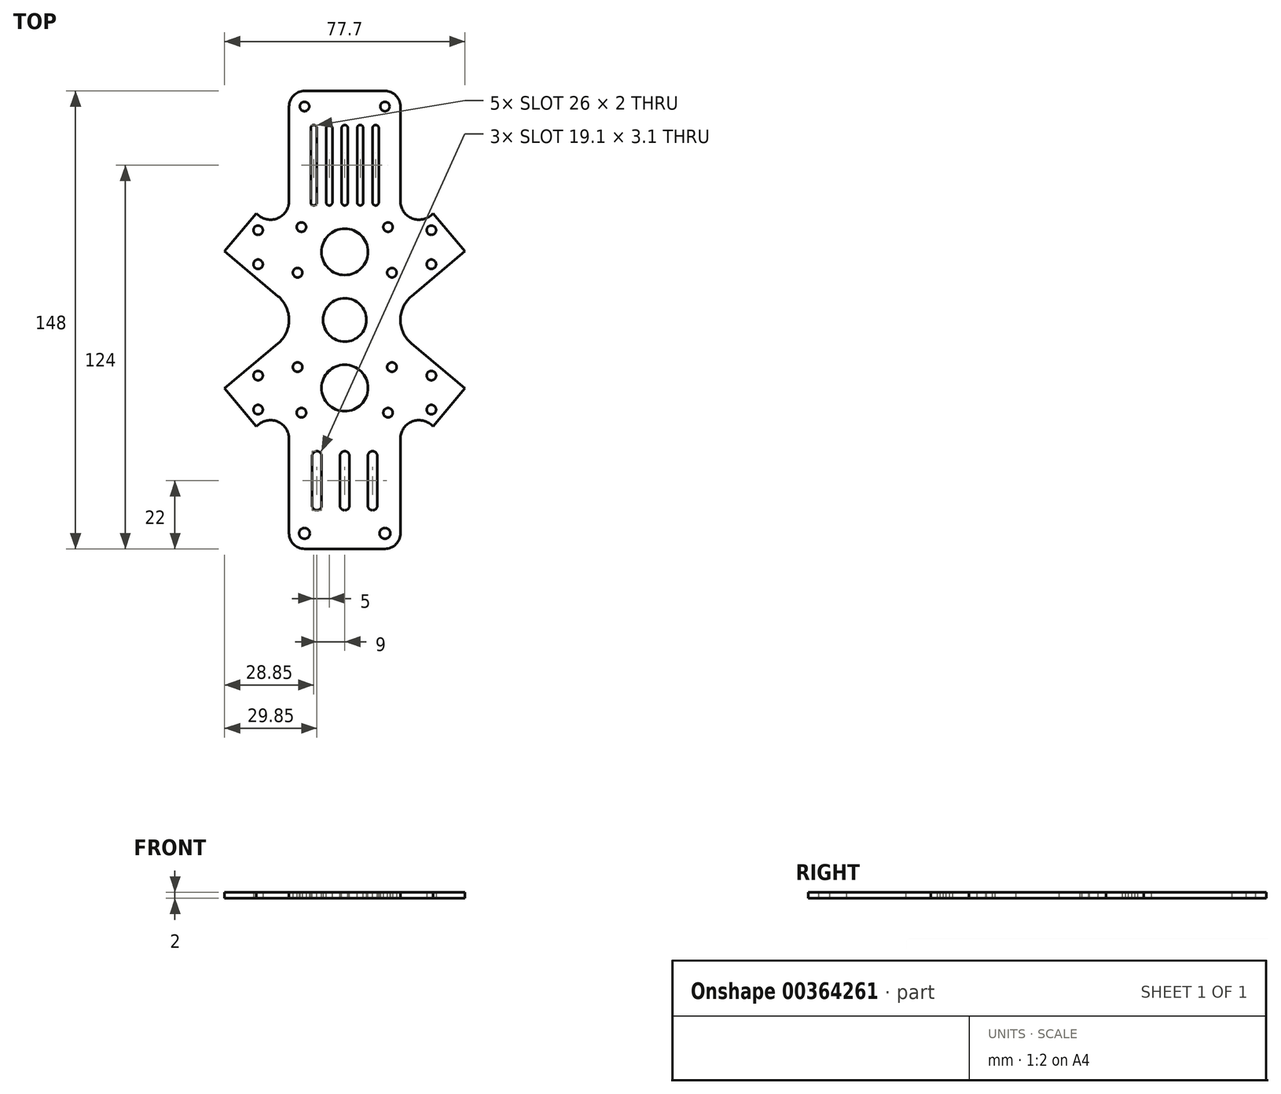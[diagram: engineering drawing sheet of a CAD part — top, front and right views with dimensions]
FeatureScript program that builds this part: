
annotation { "Feature Type Name" : "Feature", "Feature Type Description" : "" }
export const myFeature = defineFeature(function(context is Context, id is Id, definition is map)
    precondition{}
    {
        {
            var Q0;
            Q0=qCreatedBy(makeId("Top.planeOp"),FACE);
            var sketch = newSketch(context, id + "F0", { "sketchPlane" : qUnion([Q0])});
            skLineSegment(sketch, "E0", {"start": v(-28.56, 34.41) * mm, "end": v(-38.85, 22.15) * mm});
            skLineSegment(sketch, "E1", {"start": v(-38.85, 22.15) * mm, "end": v(-21.58, 7.66) * mm});
            skLineSegment(sketch, "E2", {"start": v(-28.56, 34.41) * mm, "end": v(-27.86, 33.82) * mm});
            skLineSegment(sketch, "E3", {"start": v(0, 74) * mm, "end": v(-13, 74) * mm});
            skLineSegment(sketch, "E4", {"start": v(-18, 69) * mm, "end": v(-18, 38.41) * mm});
            skLineSegment(sketch, "E5", {"start": v(-84.26, 70.7) * mm, "end": v(0, 0) * mm, "construction": true});
            skCircle(sketch, "E6", {"center": v(0, 0) * mm, "radius": 110 * mm, "construction": true});
            skPoint(sketch, "E7.visualSharp", {"position": v(-18, 25.55) * mm});
            skArc(sketch, "E7.filletArc", {"start": v(-27.86, 33.82) * mm, "mid": v(-21.46, 32.98) * mm, "end": v(-18, 38.41) * mm});
            skPoint(sketch, "E8.visualSharp", {"position": v(-18, 74) * mm});
            skArc(sketch, "E8.filletArc", {"start": v(-13, 74) * mm, "mid": v(-16.54, 72.54) * mm, "end": v(-18, 69) * mm});
            skCircle(sketch, "E9", {"center": v(-13, 69) * mm, "radius": 1.52 * mm});
            skCircle(sketch, "E10", {"center": v(-28, 29) * mm, "radius": 1.52 * mm});
            skCircle(sketch, "E11", {"center": v(-28, 18) * mm, "radius": 1.52 * mm});
            skCircle(sketch, "E12", {"center": v(-15.25, 15.25) * mm, "radius": 1.52 * mm});
            skCircle(sketch, "E13.MirrorC", {"center": v(13, 69) * mm, "radius": 1.52 * mm});
            skArc(sketch, "E14.MirrorCS", {"start": v(13, 74) * mm, "mid": v(16.54, 72.54) * mm, "end": v(18, 69) * mm});
            skLineSegment(sketch, "E15.MirrorCS", {"start": v(0, 74) * mm, "end": v(13, 74) * mm});
            skCircle(sketch, "E16.MirrorC", {"center": v(28, 29) * mm, "radius": 1.52 * mm});
            skCircle(sketch, "E17.MirrorC", {"center": v(15.25, 15.25) * mm, "radius": 1.52 * mm});
            skCircle(sketch, "E18.MirrorC", {"center": v(28, 18) * mm, "radius": 1.52 * mm});
            skPoint(sketch, "E19.MirrorP", {"position": v(18, 25.55) * mm});
            skLineSegment(sketch, "E20.MirrorCS", {"start": v(28.56, 34.41) * mm, "end": v(38.85, 22.15) * mm});
            skLineSegment(sketch, "E21.MirrorCS", {"start": v(18, 69) * mm, "end": v(18, 38.41) * mm});
            skLineSegment(sketch, "E22.MirrorCS", {"start": v(38.85, 22.15) * mm, "end": v(21.58, 7.66) * mm});
            skLineSegment(sketch, "E23.MirrorCS", {"start": v(28.56, 34.41) * mm, "end": v(27.86, 33.82) * mm});
            skArc(sketch, "E24.MirrorCS", {"start": v(27.86, 33.82) * mm, "mid": v(21.46, 32.98) * mm, "end": v(18, 38.41) * mm});
            skPoint(sketch, "E25.MirrorP", {"position": v(18, 74) * mm});
            skLineSegment(sketch, "E26.MirrorCS", {"start": v(84.26, 70.7) * mm, "end": v(0, 0) * mm, "construction": true});
            skArc(sketch, "E27.MirrorCS", {"start": v(-13, -74) * mm, "mid": v(-16.54, -72.54) * mm, "end": v(-18, -69) * mm});
            skCircle(sketch, "E28.MirrorC", {"center": v(-28, -18) * mm, "radius": 1.52 * mm});
            skCircle(sketch, "E29.MirrorC", {"center": v(28, -29) * mm, "radius": 1.52 * mm});
            skCircle(sketch, "E30.MirrorC", {"center": v(-15.25, -15.25) * mm, "radius": 1.52 * mm});
            skCircle(sketch, "E31.MirrorC", {"center": v(15.25, -15.25) * mm, "radius": 1.52 * mm});
            skLineSegment(sketch, "E32.MirrorCS", {"start": v(0, -74) * mm, "end": v(-13, -74) * mm});
            skCircle(sketch, "E33.MirrorC", {"center": v(28, -18) * mm, "radius": 1.52 * mm});
            skArc(sketch, "E34.MirrorCS", {"start": v(13, -74) * mm, "mid": v(16.54, -72.54) * mm, "end": v(18, -69) * mm});
            skCircle(sketch, "E35.MirrorC", {"center": v(-28, -29) * mm, "radius": 1.52 * mm});
            skPoint(sketch, "E36.MirrorP", {"position": v(-18, -25.55) * mm});
            skArc(sketch, "E37.MirrorCS", {"start": v(-27.86, -33.82) * mm, "mid": v(-21.46, -32.98) * mm, "end": v(-18, -38.41) * mm});
            skArc(sketch, "E38.MirrorCS", {"start": v(27.86, -33.82) * mm, "mid": v(21.46, -32.98) * mm, "end": v(18, -38.41) * mm});
            skLineSegment(sketch, "E39.MirrorCS", {"start": v(-38.85, -22.15) * mm, "end": v(-21.58, -7.66) * mm});
            skLineSegment(sketch, "E40.MirrorCS", {"start": v(0, -74) * mm, "end": v(13, -74) * mm});
            skPoint(sketch, "E41.MirrorP", {"position": v(18, -25.55) * mm});
            skPoint(sketch, "E42.MirrorP", {"position": v(18, -74) * mm});
            skLineSegment(sketch, "E43.MirrorCS", {"start": v(-28.56, -34.41) * mm, "end": v(-27.86, -33.82) * mm});
            skPoint(sketch, "E44.MirrorP", {"position": v(-18, -74) * mm});
            skLineSegment(sketch, "E45.MirrorCS", {"start": v(-18, -69) * mm, "end": v(-18, -38.41) * mm});
            skLineSegment(sketch, "E46.MirrorCS", {"start": v(18, -69) * mm, "end": v(18, -38.41) * mm});
            skLineSegment(sketch, "E47.MirrorCS", {"start": v(38.85, -22.15) * mm, "end": v(21.58, -7.66) * mm});
            skLineSegment(sketch, "E48.MirrorCS", {"start": v(28.56, -34.41) * mm, "end": v(38.85, -22.15) * mm});
            skLineSegment(sketch, "E49.MirrorCS", {"start": v(-28.56, -34.41) * mm, "end": v(-38.85, -22.15) * mm});
            skLineSegment(sketch, "E50.MirrorCS", {"start": v(28.56, -34.41) * mm, "end": v(27.86, -33.82) * mm});
            skPoint(sketch, "E51.visualSharp", {"position": v(-12.45, 0) * mm});
            skArc(sketch, "E51.filletArc", {"start": v(-21.58, -7.66) * mm, "mid": v(-18, 0) * mm, "end": v(-21.58, 7.66) * mm});
            skPoint(sketch, "E52.visualSharp", {"position": v(12.45, 0) * mm});
            skArc(sketch, "E52.filletArc", {"start": v(21.58, 7.66) * mm, "mid": v(18, 0) * mm, "end": v(21.58, -7.66) * mm});
            skCircle(sketch, "E53", {"center": v(-84.26, 70.7) * mm, "radius": 64.5 * mm, "construction": true});
            skCircle(sketch, "E54", {"center": v(-14, 30) * mm, "radius": 1.52 * mm});
            skCircle(sketch, "E55.MirrorC", {"center": v(14, 30) * mm, "radius": 1.52 * mm});
            skCircle(sketch, "E56.MirrorC", {"center": v(-14, -30) * mm, "radius": 1.52 * mm});
            skCircle(sketch, "E57.MirrorC", {"center": v(14, -30) * mm, "radius": 1.52 * mm});
            skCircle(sketch, "E58", {"center": v(-13, -69) * mm, "radius": 1.75 * mm});
            skCircle(sketch, "E59.MirrorC", {"center": v(13, -69) * mm, "radius": 1.75 * mm});
            skCircle(sketch, "E60", {"center": v(0, 0) * mm, "radius": 7 * mm});
            skSolve(sketch);
        }
        {
            var Q0;
            Q0 = qSketchRegion(id + "F0", true);
            extrude(context, id + "F1", {"entities" : qUnion([Q0]), "depth" : 2 * mm});
        }
        {
            var Q0;
            Q0=makeQuery(id+"F1.opExtrude","CAP_FACE",FACE,{"disambiguationData":[OSD([sQuery(id+"F0.wireOp",EDGE,"E0"),sQuery(id+"F0.wireOp",EDGE,"E1"),sQuery(id+"F0.wireOp",EDGE,"E2"),sQuery(id+"F0.wireOp",EDGE,"E3"),sQuery(id+"F0.wireOp",EDGE,"E4"),sQuery(id+"F0.wireOp",EDGE,"E7.filletArc"),sQuery(id+"F0.wireOp",EDGE,"E8.filletArc"),sQuery(id+"F0.wireOp",EDGE,"E9"),sQuery(id+"F0.wireOp",EDGE,"E10"),sQuery(id+"F0.wireOp",EDGE,"E11"),sQuery(id+"F0.wireOp",EDGE,"E12"),sQuery(id+"F0.wireOp",EDGE,"E13.MirrorC"),sQuery(id+"F0.wireOp",EDGE,"E14.MirrorCS"),sQuery(id+"F0.wireOp",EDGE,"E15.MirrorCS"),sQuery(id+"F0.wireOp",EDGE,"E16.MirrorC"),sQuery(id+"F0.wireOp",EDGE,"E17.MirrorC"),sQuery(id+"F0.wireOp",EDGE,"E18.MirrorC"),sQuery(id+"F0.wireOp",EDGE,"E20.MirrorCS"),sQuery(id+"F0.wireOp",EDGE,"E21.MirrorCS"),sQuery(id+"F0.wireOp",EDGE,"E22.MirrorCS"),sQuery(id+"F0.wireOp",EDGE,"E23.MirrorCS"),sQuery(id+"F0.wireOp",EDGE,"E24.MirrorCS"),sQuery(id+"F0.wireOp",EDGE,"E27.MirrorCS"),sQuery(id+"F0.wireOp",EDGE,"E28.MirrorC"),sQuery(id+"F0.wireOp",EDGE,"E29.MirrorC"),sQuery(id+"F0.wireOp",EDGE,"E30.MirrorC"),sQuery(id+"F0.wireOp",EDGE,"E31.MirrorC"),sQuery(id+"F0.wireOp",EDGE,"E32.MirrorCS"),sQuery(id+"F0.wireOp",EDGE,"E33.MirrorC"),sQuery(id+"F0.wireOp",EDGE,"E34.MirrorCS"),sQuery(id+"F0.wireOp",EDGE,"E35.MirrorC"),sQuery(id+"F0.wireOp",EDGE,"E37.MirrorCS"),sQuery(id+"F0.wireOp",EDGE,"E38.MirrorCS"),sQuery(id+"F0.wireOp",EDGE,"E39.MirrorCS"),sQuery(id+"F0.wireOp",EDGE,"E40.MirrorCS"),sQuery(id+"F0.wireOp",EDGE,"E43.MirrorCS"),sQuery(id+"F0.wireOp",EDGE,"E45.MirrorCS"),sQuery(id+"F0.wireOp",EDGE,"E46.MirrorCS"),sQuery(id+"F0.wireOp",EDGE,"E47.MirrorCS"),sQuery(id+"F0.wireOp",EDGE,"E48.MirrorCS"),sQuery(id+"F0.wireOp",EDGE,"E49.MirrorCS"),sQuery(id+"F0.wireOp",EDGE,"E50.MirrorCS"),sQuery(id+"F0.wireOp",EDGE,"E51.filletArc"),sQuery(id+"F0.wireOp",EDGE,"E52.filletArc"),sQuery(id+"F0.wireOp",EDGE,"E54"),sQuery(id+"F0.wireOp",EDGE,"E55.MirrorC"),sQuery(id+"F0.wireOp",EDGE,"E56.MirrorC"),sQuery(id+"F0.wireOp",EDGE,"E57.MirrorC"),sQuery(id+"F0.wireOp",EDGE,"93c6d2c4-f13a-42fa-8daf-070bf65a8a60.0.left"),sQuery(id+"F0.wireOp",EDGE,"93c6d2c4-f13a-42fa-8daf-070bf65a8a60.0.right"),sQuery(id+"F0.wireOp",EDGE,"93c6d2c4-f13a-42fa-8daf-070bf65a8a60.1.left"),sQuery(id+"F0.wireOp",EDGE,"93c6d2c4-f13a-42fa-8daf-070bf65a8a60.1.right"),sQuery(id+"F0.wireOp",EDGE,"E58"),sQuery(id+"F0.wireOp",EDGE,"E59.MirrorC"),sQuery(id+"F0.wireOp",EDGE,"E60"),sQuery(id+"F0.wireOp",EDGE,"nUquFca2-qsaJ-jwJN-5oFK-tLH4V0bp0isj"),sQuery(id+"F0.wireOp",EDGE,"GrDH1Zwj-MUL8-2ccp-gC30-TyDLYz1ijxhj"),sQuery(id+"F0.wireOp",EDGE,"lQEg5da1-VNvQ-DT9M-XKNg-c66ZYZLATFQq"),sQuery(id+"F0.wireOp",EDGE,"kMfInx9H-W6u4-GL8q-Tmun-flGKoSWlkOP9"),sQuery(id+"F0.wireOp",EDGE,"hAw3ivOI-FHfI-7WR2-swgj-VFjn3qP7wQiq"),sQuery(id+"F0.wireOp",EDGE,"v5kMoyw8-5eYl-1tFt-IAkN-Yu3lpjZkXJHz"),sQuery(id+"F0.wireOp",EDGE,"L4HZwAwQ-pxIO-Uqwo-2Bf3-76P6cPw9qCx9"),sQuery(id+"F0.wireOp",EDGE,"TBTr9jrp-s2Nj-AiS6-Zdoc-dO8zuvt9AdQ4"),sQuery(id+"F0.wireOp",EDGE,"8gbrVnR2-a2jK-DphX-z2TC-3oRPmb43RnOK"),sQuery(id+"F0.wireOp",EDGE,"ZJLvlH0n-JZwF-yflx-Rwd1-jo0cSRqBPjVH"),sQuery(id+"F0.wireOp",EDGE,"PCCi1lkv-C6qh-hLjU-n2um-C6nXSVXEERcv"),sQuery(id+"F0.wireOp",EDGE,"3Ri7i5VD-pUbN-ChsC-X1DZ-rpwYTm5fkQc2"),sQuery(id+"F0.wireOp",EDGE,"63a17562-372a-4be2-8eea-18665176cc5a0.MirrorCS"),sQuery(id+"F0.wireOp",EDGE,"63a17562-372a-4be2-8eea-18665176cc5a1.MirrorCS"),sQuery(id+"F0.wireOp",EDGE,"63a17562-372a-4be2-8eea-18665176cc5a2.MirrorCS"),sQuery(id+"F0.wireOp",EDGE,"63a17562-372a-4be2-8eea-18665176cc5a3.MirrorCS"),sQuery(id+"F0.wireOp",EDGE,"63a17562-372a-4be2-8eea-18665176cc5a4.MirrorCS"),sQuery(id+"F0.wireOp",EDGE,"63a17562-372a-4be2-8eea-18665176cc5a5.MirrorCS"),sQuery(id+"F0.wireOp",EDGE,"63a17562-372a-4be2-8eea-18665176cc5a6.MirrorCS"),sQuery(id+"F0.wireOp",EDGE,"63a17562-372a-4be2-8eea-18665176cc5a7.MirrorCS"),sQuery(id+"F0.wireOp",EDGE,"63a17562-372a-4be2-8eea-18665176cc5a8.MirrorCS"),sQuery(id+"F0.wireOp",EDGE,"63a17562-372a-4be2-8eea-18665176cc5a9.MirrorCS"),sQuery(id+"F0.wireOp",EDGE,"63a17562-372a-4be2-8eea-18665176cc5a10.MirrorCS"),sQuery(id+"F0.wireOp",EDGE,"63a17562-372a-4be2-8eea-18665176cc5a11.MirrorCS"),sQuery(id+"F0.wireOp",EDGE,"63a17562-372a-4be2-8eea-18665176cc5a12.MirrorCS"),sQuery(id+"F0.wireOp",EDGE,"63a17562-372a-4be2-8eea-18665176cc5a13.MirrorCS"),sQuery(id+"F0.wireOp",EDGE,"63a17562-372a-4be2-8eea-18665176cc5a16.MirrorCS"),sQuery(id+"F0.wireOp",EDGE,"63a17562-372a-4be2-8eea-18665176cc5a17.MirrorCS")])],"isStart":false});
            var sketch = newSketch(context, id + "F2", { "sketchPlane" : qUnion([Q0])});
            skCircle(sketch, "E61", {"center": v(0, -22) * mm, "radius": 7.5 * mm});
            skCircle(sketch, "E62", {"center": v(0, 22) * mm, "radius": 7.5 * mm});
            skLineSegment(sketch, "E63", {"start": v(-18, 50) * mm, "end": v(18, 50) * mm, "construction": true});
            skLineSegment(sketch, "E64", {"start": v(-9, -44) * mm, "end": v(-9, -60) * mm, "construction": true});
            skLineSegment(sketch, "E65", {"start": v(0, -44) * mm, "end": v(0, -60) * mm, "construction": true});
            skLineSegment(sketch, "E66", {"start": v(9, -44) * mm, "end": v(9, -60) * mm, "construction": true});
            skArc(sketch, "E67.0.startCap", {"start": v(-10.55, -44) * mm, "mid": v(-9, -42.45) * mm, "end": v(-7.45, -44) * mm});
            skArc(sketch, "E67.0.endCap", {"start": v(-7.45, -60) * mm, "mid": v(-9, -61.55) * mm, "end": v(-10.55, -60) * mm});
            skLineSegment(sketch, "E67.0.left", {"start": v(-7.45, -44) * mm, "end": v(-7.45, -60) * mm});
            skLineSegment(sketch, "E67.0.right", {"start": v(-10.55, -44) * mm, "end": v(-10.55, -60) * mm});
            skArc(sketch, "E68.0.startCap", {"start": v(-1.55, -44) * mm, "mid": v(0, -42.45) * mm, "end": v(1.55, -44) * mm});
            skArc(sketch, "E68.0.endCap", {"start": v(1.55, -60) * mm, "mid": v(0, -61.55) * mm, "end": v(-1.55, -60) * mm});
            skLineSegment(sketch, "E68.0.left", {"start": v(1.55, -44) * mm, "end": v(1.55, -60) * mm});
            skLineSegment(sketch, "E68.0.right", {"start": v(-1.55, -44) * mm, "end": v(-1.55, -60) * mm});
            skArc(sketch, "E68.1.startCap", {"start": v(7.45, -44) * mm, "mid": v(9, -42.45) * mm, "end": v(10.55, -44) * mm});
            skArc(sketch, "E68.1.endCap", {"start": v(10.55, -60) * mm, "mid": v(9, -61.55) * mm, "end": v(7.45, -60) * mm});
            skLineSegment(sketch, "E68.1.left", {"start": v(10.55, -44) * mm, "end": v(10.55, -60) * mm});
            skLineSegment(sketch, "E68.1.right", {"start": v(7.45, -44) * mm, "end": v(7.45, -60) * mm});
            skLineSegment(sketch, "E69", {"start": v(-10, 62) * mm, "end": v(-10, 38) * mm, "construction": true});
            skLineSegment(sketch, "E70.1.0.0", {"start": v(-5, 62) * mm, "end": v(-5, 38) * mm, "construction": true});
            skLineSegment(sketch, "E70.2.0.0", {"start": v(0, 62) * mm, "end": v(0, 38) * mm, "construction": true});
            skLineSegment(sketch, "E70.3.0.0", {"start": v(5, 62) * mm, "end": v(5, 38) * mm, "construction": true});
            skLineSegment(sketch, "E70.4.0.0", {"start": v(10, 62) * mm, "end": v(10, 38) * mm, "construction": true});
            skLineSegment(sketch, "E70.direction1", {"start": v(-10, 38) * mm, "end": v(-5, 38) * mm, "construction": true});
            skArc(sketch, "E71.0.startCap", {"start": v(-11, 62) * mm, "mid": v(-10, 63) * mm, "end": v(-9, 62) * mm});
            skArc(sketch, "E71.0.endCap", {"start": v(-9, 38) * mm, "mid": v(-10, 37) * mm, "end": v(-11, 38) * mm});
            skLineSegment(sketch, "E71.0.left", {"start": v(-9, 62) * mm, "end": v(-9, 38) * mm});
            skLineSegment(sketch, "E71.0.right", {"start": v(-11, 62) * mm, "end": v(-11, 38) * mm});
            skArc(sketch, "E72.0.startCap", {"start": v(-6, 62) * mm, "mid": v(-5, 63) * mm, "end": v(-4, 62) * mm});
            skArc(sketch, "E72.0.endCap", {"start": v(-4, 38) * mm, "mid": v(-5, 37) * mm, "end": v(-6, 38) * mm});
            skLineSegment(sketch, "E72.0.left", {"start": v(-4, 62) * mm, "end": v(-4, 38) * mm});
            skLineSegment(sketch, "E72.0.right", {"start": v(-6, 62) * mm, "end": v(-6, 38) * mm});
            skArc(sketch, "E72.1.startCap", {"start": v(-1, 62) * mm, "mid": v(0, 63) * mm, "end": v(1, 62) * mm});
            skArc(sketch, "E72.1.endCap", {"start": v(1, 38) * mm, "mid": v(0, 37) * mm, "end": v(-1, 38) * mm});
            skLineSegment(sketch, "E72.1.left", {"start": v(1, 62) * mm, "end": v(1, 38) * mm});
            skLineSegment(sketch, "E72.1.right", {"start": v(-1, 62) * mm, "end": v(-1, 38) * mm});
            skArc(sketch, "E72.2.startCap", {"start": v(4, 62) * mm, "mid": v(5, 63) * mm, "end": v(6, 62) * mm});
            skArc(sketch, "E72.2.endCap", {"start": v(6, 38) * mm, "mid": v(5, 37) * mm, "end": v(4, 38) * mm});
            skLineSegment(sketch, "E72.2.left", {"start": v(6, 62) * mm, "end": v(6, 38) * mm});
            skLineSegment(sketch, "E72.2.right", {"start": v(4, 62) * mm, "end": v(4, 38) * mm});
            skArc(sketch, "E72.3.startCap", {"start": v(9, 62) * mm, "mid": v(10, 63) * mm, "end": v(11, 62) * mm});
            skArc(sketch, "E72.3.endCap", {"start": v(11, 38) * mm, "mid": v(10, 37) * mm, "end": v(9, 38) * mm});
            skLineSegment(sketch, "E72.3.left", {"start": v(11, 62) * mm, "end": v(11, 38) * mm});
            skLineSegment(sketch, "E72.3.right", {"start": v(9, 62) * mm, "end": v(9, 38) * mm});
            skSolve(sketch);
        }
        {
            var Q0;
            Q0 = qSketchRegion(id + "F2", true);
            extrude(context, id + "F3", {"entities" : qUnion([Q0]), "operationType" : NewBodyOperationType.REMOVE, "oppositeDirection" : true, "depth" : 25 * mm, "offsetDistance" : 25 * mm});
        }
    });
